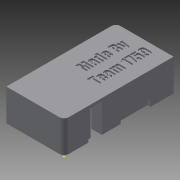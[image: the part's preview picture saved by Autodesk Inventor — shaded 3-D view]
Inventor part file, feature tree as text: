
AUTODESK INVENTOR PART (.ipt)
format: ipt  version: 2015 (Build 190159000, 159)  size: 555,008 bytes
history: native  units: in
note: dims shown in document units (in); Inventor stores cm internally (conversion verified against a paired STEP export)
features: extrude x10, sketch x9, projected_geometry x3, fillet x2
ambient origin geometry x8: Origin, YZ Plane, XZ Plane, XY Plane, X Axis, Y Axis, Z Axis, Center Point
bodies: Solid1 (feature_tree)
feature tree (24):
  extrude  "Extrusion1"  Depth=0.966in
  sketch  "Sketch2"  dims[d5=0.075in d6=0.1in d7=0.1in]
  fillet  "Fillet1"  Radius=0.533in
  fillet  "Fillet2"  Radius=0.075in
  extrude  "Extrusion2"  Depth=0.1in
  extrude  "Extrusion3"  Depth=0.125in
  extrude  "Extrusion4"  Depth=0.1in
  sketch  "Sketch6"  dims[d15=0.1in d16=0.1in]
  extrude  "Extrusion5"  Depth=0.1in
  sketch  "Sketch7"  dims[d17=0.1in d18=0.483in]
  extrude  "Extrusion7"  Depth=0.483in
  extrude  "Extrusion8"  Depth=0.1in
  extrude  "Extrusion9"  Depth=0.1in
  extrude  "Extrusion10"  Depth=0.5in
  extrude  "Extrusion11"  Depth=0.45in
  sketch  "Sketch1"  dims[d0=1.833in d1=0.966in d2=0.533in d3=0.0in d4=0.075in]
  sketch  "Sketch4"  dims[d8=0.1in d9=0.1in d11=0.125in]
  sketch  "Sketch5"  dims[d13=0.175in d14=0.1in]
  sketch  "Sketch8"  dims[d19=0.0in d20=0.1in]
  projected_geometry  "Projected Loop1"
  sketch  "Sketch9"  dims[d21=0.24in d22=0.1in]
  projected_geometry  "Projected Loop2"
  sketch  "Sketch10"  dims[d23=0.555in d24=0.5in d25=0.45in d26=0.9in d27=0.533in d28=0.0in d29=0.279in d30=0.185in d32=0.3in d33=0.1in d34=0.533in d35=0.0in d36=0.1718in d37=1.2625in d38=0.025in d39=0.0in d40=0.05in d41=0.1in d42=0.025in d43=0.025in d46=0.05in d47=0.025in d48=0.0in d49=0.025in d50=0.0in d51=0.1in d52=0.5in d53=0.05in d54=0.0in d55=0.1in d56=0.0in d57=1.0in d58=0.5in d59=0.025in d60=0.0in d61=0.375in]
  projected_geometry  "Projected Loop3"
